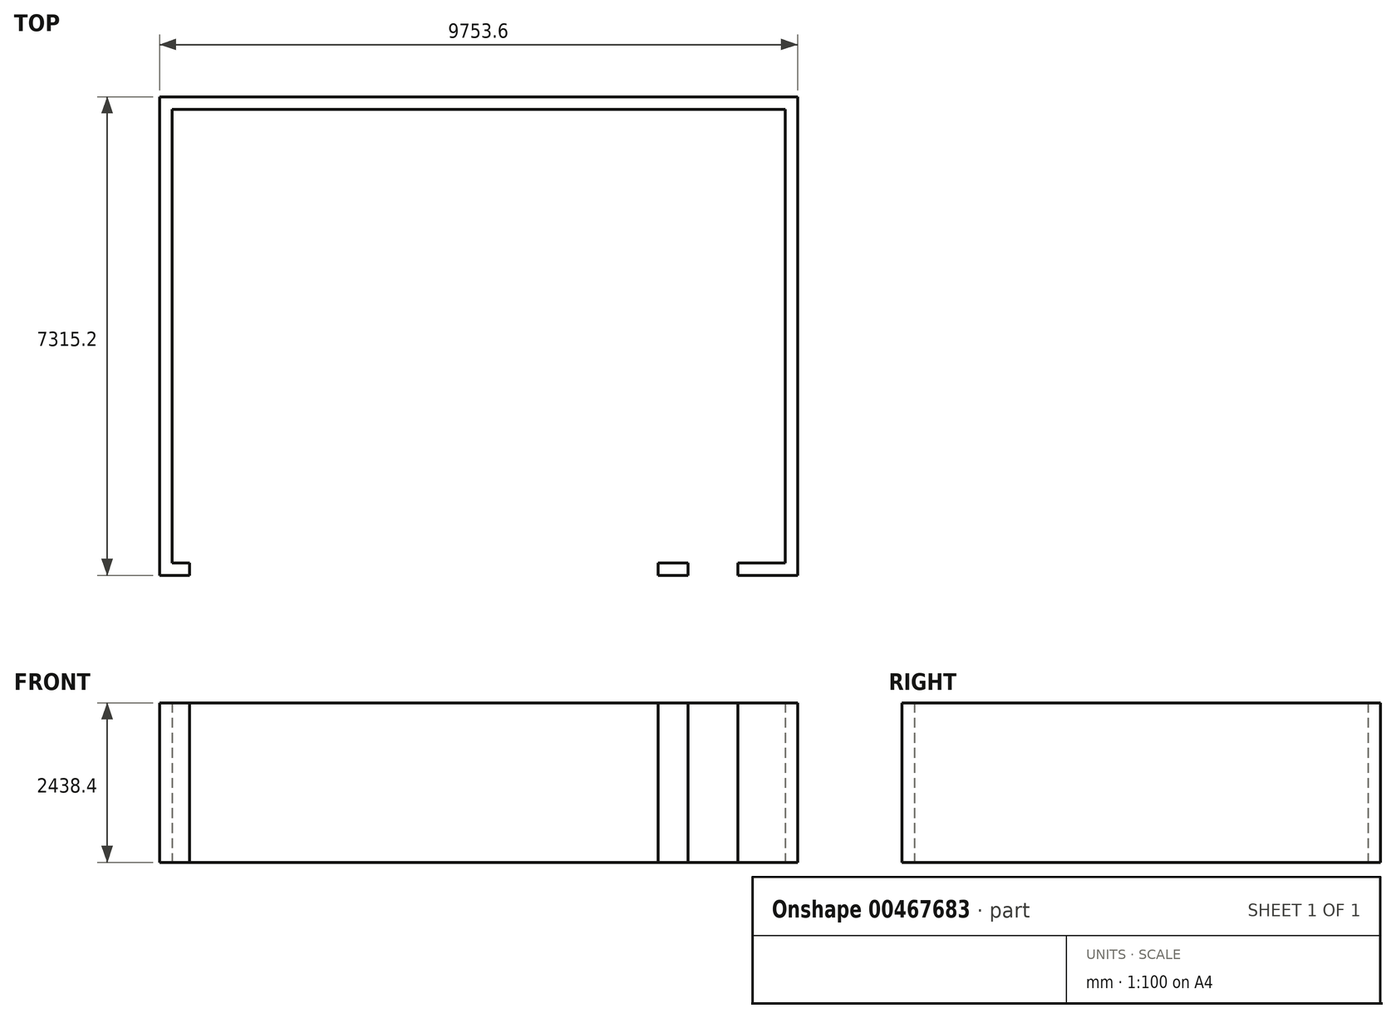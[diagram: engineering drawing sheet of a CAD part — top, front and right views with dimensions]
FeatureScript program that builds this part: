
annotation { "Feature Type Name" : "Feature", "Feature Type Description" : "" }
export const myFeature = defineFeature(function(context is Context, id is Id, definition is map)
    precondition{}
    {
        {
            var Q0;
            Q0=qCreatedBy(makeId("Top.planeOp"),FACE);
            var sketch = newSketch(context, id + "F0", { "sketchPlane" : qUnion([Q0])});
            skLineSegment(sketch, "E0.bottom", {"start": v(0, 0) * mm, "end": v(-9753.6, 0) * mm});
            skLineSegment(sketch, "E0.top", {"start": v(0, 7315.2) * mm, "end": v(-9753.6, 7315.2) * mm});
            skLineSegment(sketch, "E0.left", {"start": v(0, 0) * mm, "end": v(0, 7315.2) * mm});
            skLineSegment(sketch, "E0.right", {"start": v(-9753.6, 0) * mm, "end": v(-9753.6, 7315.2) * mm});
            skSolve(sketch);
        }
        {
            var Q0;
            Q0=makeQuery(id+"F0.imprint","IMPRINT",FACE,{"disambiguationData":[TD([[makeQuery(id+"F0.imprint","IMPRINT",EDGE,{"derivedFrom":sQuery(id+"F0.wireOp",EDGE,"E0.bottom")}),-1.0]])]});
            var sketch = newSketch(context, id + "F1", { "sketchPlane" : qUnion([Q0])});
            skPoint(sketch, "E1.orphan", {"position": v(0, 200.64) * mm});
            skLineSegment(sketch, "E2.bottom", {"start": v(1969.94, 11209.73) * mm, "end": v(11723.54, 11209.73) * mm});
            skLineSegment(sketch, "E2.top", {"start": v(1969.94, 3894.53) * mm, "end": v(2427.14, 3894.53) * mm});
            skLineSegment(sketch, "E2.left", {"start": v(1969.94, 11209.73) * mm, "end": v(1969.94, 3894.53) * mm});
            skLineSegment(sketch, "E2.right", {"start": v(11723.54, 11209.73) * mm, "end": v(11723.54, 3894.53) * mm});
            skLineSegment(sketch, "E3.0", {"start": v(2160.44, 4085.03) * mm, "end": v(11533.04, 4085.03) * mm});
            skLineSegment(sketch, "E3.1", {"start": v(11533.04, 11019.23) * mm, "end": v(11533.04, 4085.03) * mm});
            skLineSegment(sketch, "E3.2", {"start": v(2160.44, 11019.23) * mm, "end": v(11533.04, 11019.23) * mm});
            skLineSegment(sketch, "E4.0", {"start": v(2160.44, 11019.23) * mm, "end": v(2160.44, 4085.03) * mm});
            skLineSegment(sketch, "E5.0", {"start": v(1964.94, 11209.73) * mm, "end": v(1964.94, 3894.53) * mm});
            skLineSegment(sketch, "E6.trimOffspring", {"start": v(9589.94, 4085.03) * mm, "end": v(9589.94, 3894.53) * mm});
            skLineSegment(sketch, "E7.trimOffspring", {"start": v(2427.14, 4085.03) * mm, "end": v(2427.14, 3894.53) * mm});
            skLineSegment(sketch, "E8.0", {"start": v(10047.14, 4085.03) * mm, "end": v(10047.14, 3894.53) * mm});
            skLineSegment(sketch, "E9.0", {"start": v(10809.14, 4085.03) * mm, "end": v(10809.14, 3894.53) * mm});
            skLineSegment(sketch, "E10.trimOffspring", {"start": v(9589.94, 3894.53) * mm, "end": v(11723.54, 3894.53) * mm});
            skLineSegment(sketch, "E11", {"start": v(10809.14, 4085.03) * mm, "end": v(10150, 4467.37) * mm});
            skArc(sketch, "E12", {"start": v(10047.14, 4085.03) * mm, "mid": v(10073.3, 4283) * mm, "end": v(10150, 4467.37) * mm});
            skSolve(sketch);
        }
        {
            var Q0;
            {var subQ0=sQuery(id+"F1.wireOp",EDGE,"E6.trimOffspring");Q0=makeQuery(id+"F1.imprint","IMPRINT",FACE,{"disambiguationData":[TD([[makeQuery(id+"F1.imprint","IMPRINT",EDGE,{"derivedFrom":subQ0}),1.0]])]});}
            var Q1;
            Q1=makeQuery(id+"F1.imprint","IMPRINT",FACE,{"disambiguationData":[TD([[makeQuery(id+"F1.imprint","IMPRINT",EDGE,{"derivedFrom":sQuery(id+"F1.wireOp",EDGE,"E2.bottom")}),-1.0]])]});
            extrude(context, id + "F2", {"entities" : qUnion([Q0, Q1]), "depth" : 2438.4 * mm});
        }
    });
